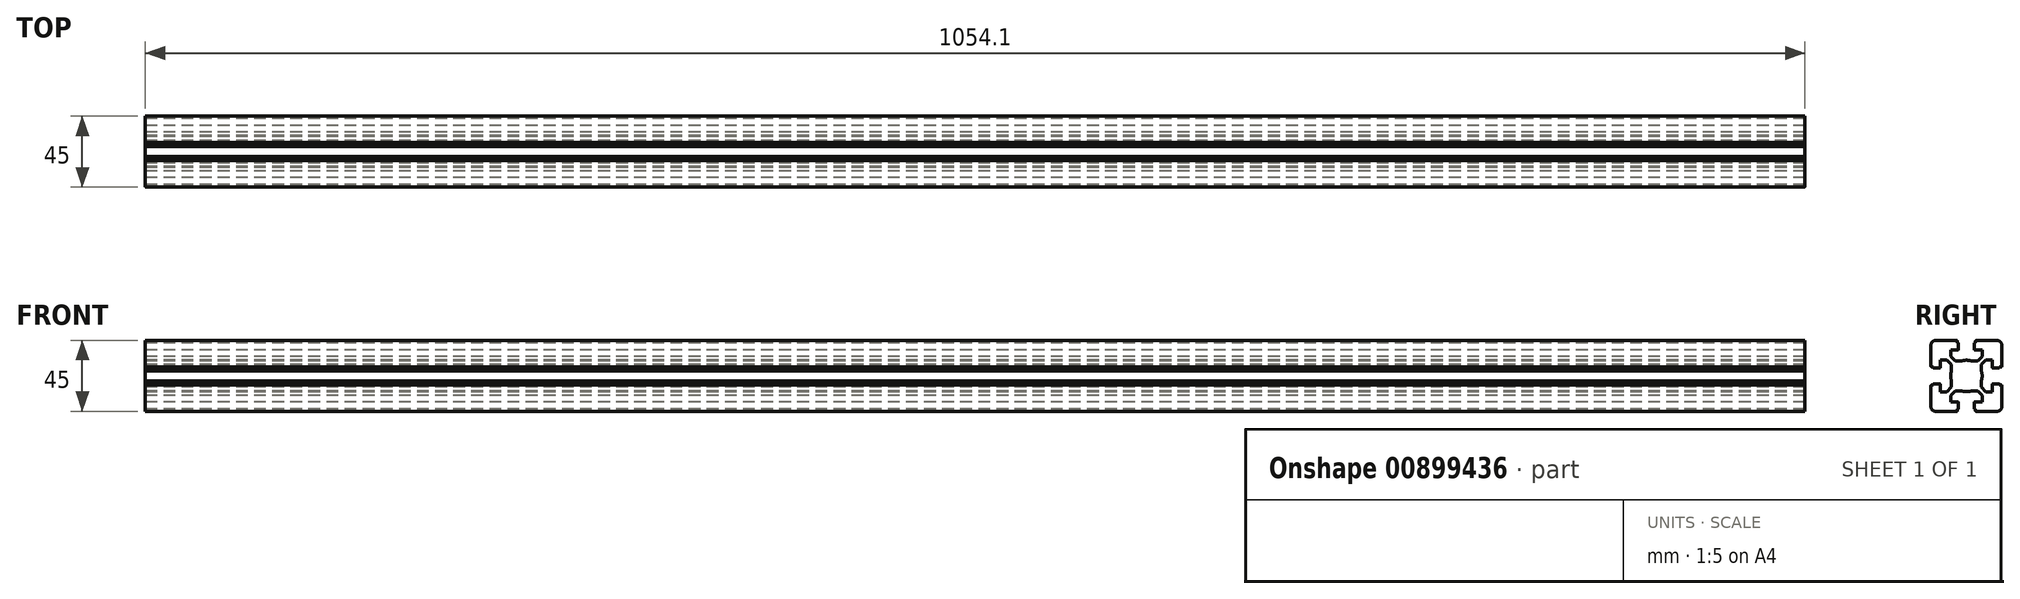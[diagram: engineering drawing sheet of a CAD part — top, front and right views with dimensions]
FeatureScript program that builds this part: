
annotation { "Feature Type Name" : "Feature", "Feature Type Description" : "" }
export const myFeature = defineFeature(function(context is Context, id is Id, definition is map)
    precondition{}
    {
        {
            var Q0;
            Q0=qCreatedBy(makeId("Right.planeOp"),FACE);
            var sketch = newSketch(context, id + "F0", { "sketchPlane" : qUnion([Q0])});
            skLineSegment(sketch, "E0", {"start": v(-20.09, -10.29) * mm, "end": v(-21.29, -10.29) * mm});
            skArc(sketch, "E1", {"start": v(-21.29, -10.29) * mm, "mid": v(-21.5, -10.38) * mm, "end": v(-21.59, -10.59) * mm});
            skLineSegment(sketch, "E2", {"start": v(-21.59, -10.59) * mm, "end": v(-21.59, -23.99) * mm});
            skArc(sketch, "E3", {"start": v(-21.59, -23.99) * mm, "mid": v(-20.7, -26.11) * mm, "end": v(-18.59, -26.99) * mm});
            skLineSegment(sketch, "E4", {"start": v(-18.59, -26.99) * mm, "end": v(-5.19, -26.99) * mm});
            skArc(sketch, "E5", {"start": v(-5.19, -26.99) * mm, "mid": v(-4.98, -26.9) * mm, "end": v(-4.89, -26.69) * mm});
            skLineSegment(sketch, "E6", {"start": v(-4.89, -26.69) * mm, "end": v(-4.89, -25.49) * mm});
            skLineSegment(sketch, "E7", {"start": v(-4.89, -25.49) * mm, "end": v(-4.39, -25.49) * mm});
            skArc(sketch, "E8", {"start": v(-4.39, -25.49) * mm, "mid": v(-4.18, -25.4) * mm, "end": v(-4.09, -25.19) * mm});
            skLineSegment(sketch, "E9", {"start": v(-4.09, -25.19) * mm, "end": v(-4.09, -21.29) * mm});
            skArc(sketch, "E10", {"start": v(-4.09, -21.29) * mm, "mid": v(-4.18, -21.08) * mm, "end": v(-4.39, -20.99) * mm});
            skLineSegment(sketch, "E11", {"start": v(-4.39, -20.99) * mm, "end": v(-9.14, -20.99) * mm});
            skLineSegment(sketch, "E12", {"start": v(-9.14, -20.99) * mm, "end": v(-9.14, -16.88) * mm});
            skLineSegment(sketch, "E13", {"start": v(-9.14, -16.88) * mm, "end": v(-6.25, -13.99) * mm});
            skLineSegment(sketch, "E14", {"start": v(-6.25, -13.99) * mm, "end": v(-2.21, -13.99) * mm});
            skArc(sketch, "E15", {"start": v(-2.21, -13.99) * mm, "mid": v(0.91, -14.49) * mm, "end": v(4.03, -13.99) * mm});
            skLineSegment(sketch, "E16", {"start": v(-20.09, -10.29) * mm, "end": v(-20.09, -9.79) * mm});
            skArc(sketch, "E17", {"start": v(-20.09, -9.79) * mm, "mid": v(-20, -9.58) * mm, "end": v(-19.79, -9.49) * mm});
            skLineSegment(sketch, "E18", {"start": v(-19.79, -9.49) * mm, "end": v(-15.89, -9.49) * mm});
            skArc(sketch, "E19", {"start": v(-15.89, -9.49) * mm, "mid": v(-15.68, -9.58) * mm, "end": v(-15.59, -9.79) * mm});
            skLineSegment(sketch, "E20", {"start": v(-15.59, -9.79) * mm, "end": v(-15.59, -14.54) * mm});
            skLineSegment(sketch, "E21", {"start": v(-15.59, -14.54) * mm, "end": v(-11.48, -14.54) * mm});
            skLineSegment(sketch, "E22", {"start": v(-11.48, -14.54) * mm, "end": v(-8.59, -11.65) * mm});
            skLineSegment(sketch, "E23", {"start": v(-8.59, -11.65) * mm, "end": v(-8.59, -7.61) * mm});
            skLineSegment(sketch, "E24", {"start": v(29.82, -4.49) * mm, "end": v(-31.05, -4.49) * mm});
            skLineSegment(sketch, "E25.MirrorCS", {"start": v(6.71, -25.49) * mm, "end": v(6.21, -25.49) * mm});
            skArc(sketch, "E26.MirrorCS", {"start": v(7.01, -26.99) * mm, "mid": v(6.8, -26.9) * mm, "end": v(6.71, -26.69) * mm});
            skLineSegment(sketch, "E27.MirrorCS", {"start": v(10.41, -11.65) * mm, "end": v(10.41, -7.61) * mm});
            skArc(sketch, "E28.MirrorCS", {"start": v(6.21, -25.49) * mm, "mid": v(6, -25.4) * mm, "end": v(5.91, -25.19) * mm});
            skLineSegment(sketch, "E29.MirrorCS", {"start": v(6.71, -26.69) * mm, "end": v(6.71, -25.49) * mm});
            skArc(sketch, "E30.MirrorCS", {"start": v(5.91, -21.29) * mm, "mid": v(6, -21.08) * mm, "end": v(6.21, -20.99) * mm});
            skLineSegment(sketch, "E31.MirrorCS", {"start": v(10.96, -16.88) * mm, "end": v(8.07, -13.99) * mm});
            skLineSegment(sketch, "E32.MirrorCS", {"start": v(13.3, -14.54) * mm, "end": v(10.41, -11.65) * mm});
            skLineSegment(sketch, "E33.MirrorCS", {"start": v(17.41, -14.54) * mm, "end": v(13.3, -14.54) * mm});
            skLineSegment(sketch, "E34.MirrorCS", {"start": v(17.41, -9.79) * mm, "end": v(17.41, -14.54) * mm});
            skLineSegment(sketch, "E35.MirrorCS", {"start": v(6.21, -20.99) * mm, "end": v(10.96, -20.99) * mm});
            skLineSegment(sketch, "E36.MirrorCS", {"start": v(8.07, -13.99) * mm, "end": v(4.03, -13.99) * mm});
            skArc(sketch, "E37.MirrorCS", {"start": v(4.03, -13.99) * mm, "mid": v(0.91, -14.49) * mm, "end": v(-2.21, -13.99) * mm});
            skLineSegment(sketch, "E38.MirrorCS", {"start": v(10.96, -20.99) * mm, "end": v(10.96, -16.88) * mm});
            skLineSegment(sketch, "E39.MirrorCS", {"start": v(5.91, -25.19) * mm, "end": v(5.91, -21.29) * mm});
            skArc(sketch, "E40.MirrorCS", {"start": v(23.41, -23.99) * mm, "mid": v(22.53, -26.11) * mm, "end": v(20.41, -26.99) * mm});
            skLineSegment(sketch, "E41.MirrorCS", {"start": v(20.41, -26.99) * mm, "end": v(7.01, -26.99) * mm});
            skLineSegment(sketch, "E42.MirrorCS", {"start": v(23.41, -10.59) * mm, "end": v(23.41, -23.99) * mm});
            skArc(sketch, "E43.MirrorCS", {"start": v(17.71, -9.49) * mm, "mid": v(17.5, -9.58) * mm, "end": v(17.41, -9.79) * mm});
            skArc(sketch, "E44.MirrorCS", {"start": v(23.11, -10.29) * mm, "mid": v(23.32, -10.38) * mm, "end": v(23.41, -10.59) * mm});
            skLineSegment(sketch, "E45.MirrorCS", {"start": v(21.91, -10.29) * mm, "end": v(21.91, -9.79) * mm});
            skLineSegment(sketch, "E46.MirrorCS", {"start": v(21.91, -10.29) * mm, "end": v(23.11, -10.29) * mm});
            skArc(sketch, "E47.MirrorCS", {"start": v(21.91, -9.79) * mm, "mid": v(21.82, -9.58) * mm, "end": v(21.61, -9.49) * mm});
            skLineSegment(sketch, "E48.MirrorCS", {"start": v(21.61, -9.49) * mm, "end": v(17.71, -9.49) * mm});
            skLineSegment(sketch, "E49.MirrorCS", {"start": v(6.71, 16.51) * mm, "end": v(6.21, 16.51) * mm});
            skArc(sketch, "E50.MirrorCS", {"start": v(-4.39, 16.51) * mm, "mid": v(-4.18, 16.42) * mm, "end": v(-4.09, 16.21) * mm});
            skLineSegment(sketch, "E51.MirrorCS", {"start": v(-4.89, 16.51) * mm, "end": v(-4.39, 16.51) * mm});
            skArc(sketch, "E52.MirrorCS", {"start": v(5.91, 12.31) * mm, "mid": v(6, 12.1) * mm, "end": v(6.21, 12.01) * mm});
            skLineSegment(sketch, "E53.MirrorCS", {"start": v(6.71, 17.71) * mm, "end": v(6.71, 16.51) * mm});
            skLineSegment(sketch, "E54.MirrorCS", {"start": v(-4.89, 17.71) * mm, "end": v(-4.89, 16.51) * mm});
            skArc(sketch, "E55.MirrorCS", {"start": v(-5.19, 18.01) * mm, "mid": v(-4.98, 17.92) * mm, "end": v(-4.89, 17.71) * mm});
            skArc(sketch, "E56.MirrorCS", {"start": v(-4.09, 12.31) * mm, "mid": v(-4.18, 12.1) * mm, "end": v(-4.39, 12.01) * mm});
            skArc(sketch, "E57.MirrorCS", {"start": v(7.01, 18.01) * mm, "mid": v(6.8, 17.92) * mm, "end": v(6.71, 17.71) * mm});
            skArc(sketch, "E58.MirrorCS", {"start": v(6.21, 16.51) * mm, "mid": v(6, 16.42) * mm, "end": v(5.91, 16.21) * mm});
            skArc(sketch, "E59.MirrorCS", {"start": v(23.11, 1.31) * mm, "mid": v(23.32, 1.4) * mm, "end": v(23.41, 1.61) * mm});
            skLineSegment(sketch, "E60.MirrorCS", {"start": v(21.91, 1.31) * mm, "end": v(21.91, 0.81) * mm});
            skArc(sketch, "E61.MirrorCS", {"start": v(-15.89, 0.51) * mm, "mid": v(-15.68, 0.6) * mm, "end": v(-15.59, 0.81) * mm});
            skArc(sketch, "E62.MirrorCS", {"start": v(-21.29, 1.31) * mm, "mid": v(-21.5, 1.4) * mm, "end": v(-21.59, 1.61) * mm});
            skArc(sketch, "E63.MirrorCS", {"start": v(17.71, 0.51) * mm, "mid": v(17.5, 0.6) * mm, "end": v(17.41, 0.81) * mm});
            skArc(sketch, "E64.MirrorCS", {"start": v(21.91, 0.81) * mm, "mid": v(21.82, 0.6) * mm, "end": v(21.61, 0.51) * mm});
            skLineSegment(sketch, "E65.MirrorCS", {"start": v(21.91, 1.31) * mm, "end": v(23.11, 1.31) * mm});
            skArc(sketch, "E66.MirrorCS", {"start": v(14.31, 5.31) * mm, "mid": v(14.1, 5.4) * mm, "end": v(14.01, 5.61) * mm});
            skArc(sketch, "E67.MirrorCS", {"start": v(-20.09, 0.81) * mm, "mid": v(-20, 0.6) * mm, "end": v(-19.79, 0.51) * mm});
            skLineSegment(sketch, "E68.MirrorCS", {"start": v(-20.09, 1.31) * mm, "end": v(-21.29, 1.31) * mm});
            skLineSegment(sketch, "E69.MirrorCS", {"start": v(-20.09, 1.31) * mm, "end": v(-20.09, 0.81) * mm});
            skLineSegment(sketch, "E70.MirrorCS", {"start": v(8.07, 5.01) * mm, "end": v(4.03, 5.01) * mm});
            skLineSegment(sketch, "E71.MirrorCS", {"start": v(-4.09, 16.21) * mm, "end": v(-4.09, 12.31) * mm});
            skLineSegment(sketch, "E72.MirrorCS", {"start": v(-9.14, 12.01) * mm, "end": v(-9.14, 7.9) * mm});
            skLineSegment(sketch, "E73.MirrorCS", {"start": v(-15.59, 5.56) * mm, "end": v(-11.48, 5.56) * mm});
            skLineSegment(sketch, "E74.MirrorCS", {"start": v(-4.39, 12.01) * mm, "end": v(-9.14, 12.01) * mm});
            skLineSegment(sketch, "E75.MirrorCS", {"start": v(-9.14, 7.9) * mm, "end": v(-6.25, 5.01) * mm});
            skLineSegment(sketch, "E76.MirrorCS", {"start": v(10.96, 12.01) * mm, "end": v(10.96, 7.9) * mm});
            skArc(sketch, "E77.MirrorCS", {"start": v(-21.59, 15.01) * mm, "mid": v(-20.7, 17.13) * mm, "end": v(-18.59, 18.01) * mm});
            skLineSegment(sketch, "E78.MirrorCS", {"start": v(23.41, 1.61) * mm, "end": v(23.41, 15.01) * mm});
            skLineSegment(sketch, "E79.MirrorCS", {"start": v(13.3, 5.56) * mm, "end": v(10.41, 2.67) * mm});
            skLineSegment(sketch, "E80.MirrorCS", {"start": v(-8.59, 2.67) * mm, "end": v(-8.59, -1.37) * mm});
            skLineSegment(sketch, "E81.MirrorCS", {"start": v(-15.59, 0.81) * mm, "end": v(-15.59, 5.56) * mm});
            skLineSegment(sketch, "E82.MirrorCS", {"start": v(10.41, 2.67) * mm, "end": v(10.41, -1.37) * mm});
            skLineSegment(sketch, "E83.MirrorCS", {"start": v(-18.59, 18.01) * mm, "end": v(-5.19, 18.01) * mm});
            skLineSegment(sketch, "E84.MirrorCS", {"start": v(10.96, 7.9) * mm, "end": v(8.07, 5.01) * mm});
            skLineSegment(sketch, "E85.MirrorCS", {"start": v(17.41, 5.56) * mm, "end": v(13.3, 5.56) * mm});
            skArc(sketch, "E86.MirrorCS", {"start": v(23.41, 15.01) * mm, "mid": v(22.53, 17.13) * mm, "end": v(20.41, 18.01) * mm});
            skLineSegment(sketch, "E87.MirrorCS", {"start": v(5.91, 16.21) * mm, "end": v(5.91, 12.31) * mm});
            skLineSegment(sketch, "E88.MirrorCS", {"start": v(17.41, 0.81) * mm, "end": v(17.41, 5.56) * mm});
            skLineSegment(sketch, "E89.MirrorCS", {"start": v(-11.48, 5.56) * mm, "end": v(-8.59, 2.67) * mm});
            skLineSegment(sketch, "E90.MirrorCS", {"start": v(-6.25, 5.01) * mm, "end": v(-2.21, 5.01) * mm});
            skLineSegment(sketch, "E91.MirrorCS", {"start": v(-21.59, 1.61) * mm, "end": v(-21.59, 15.01) * mm});
            skArc(sketch, "E92.MirrorCS", {"start": v(4.03, 5.01) * mm, "mid": v(0.91, 5.51) * mm, "end": v(-2.21, 5.01) * mm});
            skLineSegment(sketch, "E93.MirrorCS", {"start": v(6.21, 12.01) * mm, "end": v(10.96, 12.01) * mm});
            skArc(sketch, "E94.MirrorCS", {"start": v(-2.21, 5.01) * mm, "mid": v(0.91, 5.51) * mm, "end": v(4.03, 5.01) * mm});
            skLineSegment(sketch, "E95.MirrorCS", {"start": v(20.41, 18.01) * mm, "end": v(7.01, 18.01) * mm});
            skLineSegment(sketch, "E96.MirrorCS", {"start": v(-19.79, 0.51) * mm, "end": v(-15.89, 0.51) * mm});
            skLineSegment(sketch, "E97.MirrorCS", {"start": v(21.61, 0.51) * mm, "end": v(17.71, 0.51) * mm});
            skLineSegment(sketch, "E98.MirrorCS", {"start": v(0.91, -27.65) * mm, "end": v(0.91, 19.82) * mm});
            skArc(sketch, "E99", {"start": v(-8.59, -1.37) * mm, "mid": v(-9.09, -4.49) * mm, "end": v(-8.59, -7.61) * mm});
            skArc(sketch, "E100", {"start": v(10.41, -7.61) * mm, "mid": v(10.91, -4.49) * mm, "end": v(10.41, -1.37) * mm});
            skSolve(sketch);
        }
        {
            var Q0;
            Q0=qSketchRegion(id+"F0",true);
            extrude(context, id + "F1", {"entities" : qUnion([Q0]), "depth" : 1054.1 * mm, "offsetDistance" : 25.4 * mm});
        }
    });
